# Revit family: FallProtection_RigidRail_Kattsafe_PurlinMount_Inline
name_source: partatom
category: Specialty Equipment
units: mm (PartAtom-declared; Revit-internal decimal feet)

## family parameters
Cut with Voids When Loaded = Yes
Enable Cutting in Views = No
Maintain Annotation Orientation = No
OmniClass Number = 23.27.71.21
Part Type = Normal
Room Calculation Point = No
Round Connector Dimension = Use Diameter
Shared = No

## types (1)
- Type 1
    Assembly Code = E1090100
    Default Elevation = 0 mm  [stored 0 ft]
    Description = Rigid rails provide significant spanning capabilities, making them very versatile where there are limited support structures. The high strength aluminium construction, along with the unique t-bolt assembly makes it a very simple and easily adaptable system to install.
    ElementType = Fall Protection
    Export Type to IFC As = IfcBuildingElementProxy
    IfcExportAs = IfcBuildingElementProxy
    IfcExportType = USERDEFINED
    InlineBraceOffset = 500 mm  [stored 1.64042 ft]
    Manufacturer = Kattsafe®
    ManufacturerOverallDepth = 300 mm  [stored 0.984252 ft]
    ManufacturerSpecCode = OH1
    ManufacturerURLProductSpecific = https://kattsafe.com.au
    Material = Aluminum_Kattsafe_Satin
    Model = OH1
    ModifiedIssue = 20240430 $
    RailHeight = 130 mm  [stored 0.426509 ft]
    Type Comments = Rigid Rail - Purlin Mount - Inline
    Type IFC Predefined Type = USERDEFINED
    URL = https://kattsafe.com.au
    Uniclass2015Code = Pr_40_70_75_29
    Uniclass2015Title = Fall arrester devices
    Uniclass2015Version = Products v1.23

note: [stored X ft] marks values corroborated as IEEE doubles in the binary element streams (Revit-internal decimal feet)

## geometry (parser evidence)
native form markers: Extrusion x5, Sweep x25
no freeform markers — native parametric forms only
